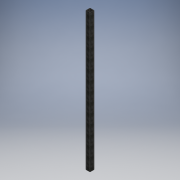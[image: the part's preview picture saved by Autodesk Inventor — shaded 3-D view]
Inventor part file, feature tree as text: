
AUTODESK INVENTOR PART (.ipt)
format: ipt  version: 2017 (Build 210142000, 142)  size: 104,448 bytes
history: native  units: mm
features: other x1, extrude x1, sketch x1
ambient origin geometry x8: Origin, YZ Plane, XZ Plane, XY Plane, X Axis, Y Axis, Z Axis, Center Point
bodies: Body1 (feature_tree)
feature tree (3):
  other  "Sólido1"
  extrude  "Extrusión1"  Depth=75.0mm
  sketch  "Boceto1"  dims[d0=75.0mm d1=75.0mm d2=3.0mm d3=37.5mm d4=37.5mm d5=2570.0mm d6=0.0mm]
